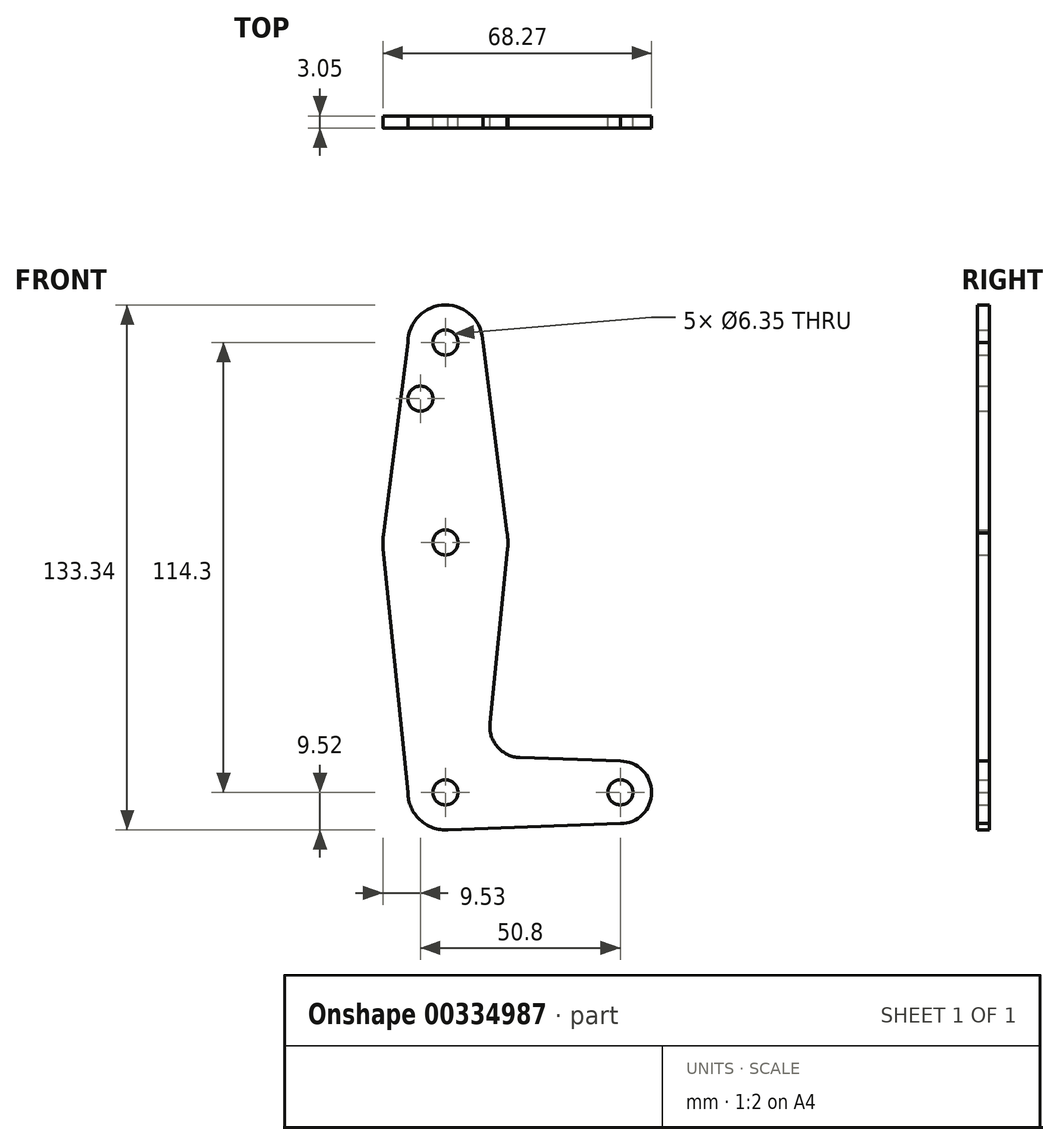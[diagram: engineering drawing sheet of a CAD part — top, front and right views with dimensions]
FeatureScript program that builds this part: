
annotation { "Feature Type Name" : "Feature", "Feature Type Description" : "" }
export const myFeature = defineFeature(function(context is Context, id is Id, definition is map)
    precondition{}
    {
        {
            var Q0;
            Q0=qCreatedBy(makeId("Front.planeOp"),FACE);
            var sketch = newSketch(context, id + "F0", { "sketchPlane" : qUnion([Q0])});
            skLineSegment(sketch, "E0", {"start": v(0, 50.8) * mm, "end": v(0, -63.5) * mm, "construction": true});
            skLineSegment(sketch, "E1", {"start": v(0, -63.5) * mm, "end": v(44.45, -63.5) * mm});
            skCircle(sketch, "E2", {"center": v(0, 50.8) * mm, "radius": 9.53 * mm});
            skCircle(sketch, "E3", {"center": v(0, 0) * mm, "radius": 15.88 * mm});
            skCircle(sketch, "E4", {"center": v(0, -63.5) * mm, "radius": 9.53 * mm});
            skCircle(sketch, "E5", {"center": v(44.45, -63.5) * mm, "radius": 7.94 * mm});
            skLineSegment(sketch, "E6", {"start": v(-9.53, 50.8) * mm, "end": v(-15.75, 2) * mm});
            skLineSegment(sketch, "E7", {"start": v(-9.52, -63.5) * mm, "end": v(-15.8, -1.6) * mm});
            skLineSegment(sketch, "E8", {"start": v(11.3, -45.9) * mm, "end": v(15.8, -1.6) * mm});
            skLineSegment(sketch, "E9", {"start": v(9.53, 50.8) * mm, "end": v(15.8, 1.6) * mm});
            skLineSegment(sketch, "E10", {"start": v(18.93, -54.65) * mm, "end": v(44.45, -55.56) * mm});
            skLineSegment(sketch, "E11", {"start": v(0, -73.02) * mm, "end": v(44.45, -71.44) * mm});
            skCircle(sketch, "E12", {"center": v(0, 50.8) * mm, "radius": 3.18 * mm});
            skCircle(sketch, "E13", {"center": v(0, 0) * mm, "radius": 3.18 * mm});
            skCircle(sketch, "E14", {"center": v(0, -63.5) * mm, "radius": 3.18 * mm});
            skCircle(sketch, "E15", {"center": v(44.45, -63.5) * mm, "radius": 3.18 * mm});
            skArc(sketch, "E16.filletArc", {"start": v(11.3, -45.9) * mm, "mid": v(13.22, -51.93) * mm, "end": v(18.93, -54.65) * mm});
            skCircle(sketch, "E17", {"center": v(-6.35, 36.53) * mm, "radius": 3.18 * mm});
            skSolve(sketch);
        }
        {
            var Q0;
            Q0 = qSketchRegion(id + "F0", true);
            extrude(context, id + "F1", {"entities" : qUnion([Q0]), "depth" : 3.05 * mm});
        }
    });
